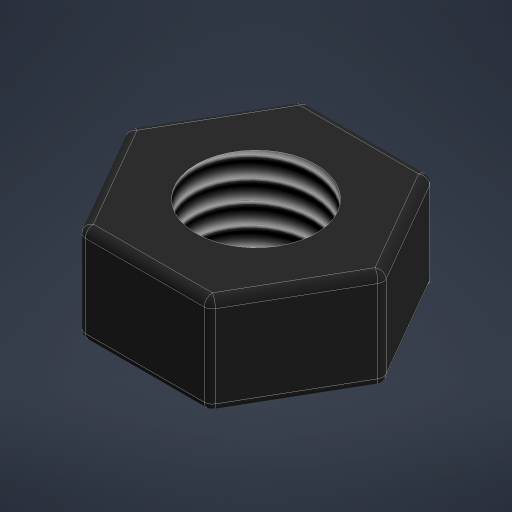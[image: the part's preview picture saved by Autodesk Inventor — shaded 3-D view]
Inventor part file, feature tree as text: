
AUTODESK INVENTOR PART (.ipt)
format: ipt  version: 2024 (Build 280153000, 153)  size: 227,840 bytes
history: native  units: mm
features: extrude x1, fillet x1, thread x1, sketch x1
ambient origin geometry x8: Origin, YZ Plane, XZ Plane, XY Plane, X Axis, Y Axis, Z Axis, Center Point
bodies: Solid1 (feature_tree)
feature tree (4):
  extrude  "Extrusion1"  Depth=0.2mm
  fillet  "Fillet1"  Radius=2.42mm
  thread  "Thread1"  [1 undecoded]
  sketch  "Sketch1"  dims[d0=5.45mm d1=2.93mm d2=2.42mm d3=0.0mm d4=0.2mm d5=2.93mm d6=0.0mm]
note: 1 required parameter value undecoded (feature->parameter linkage not recoverable at this tier; creation-order binding heuristic only, values carry confidence <= 0.55)
